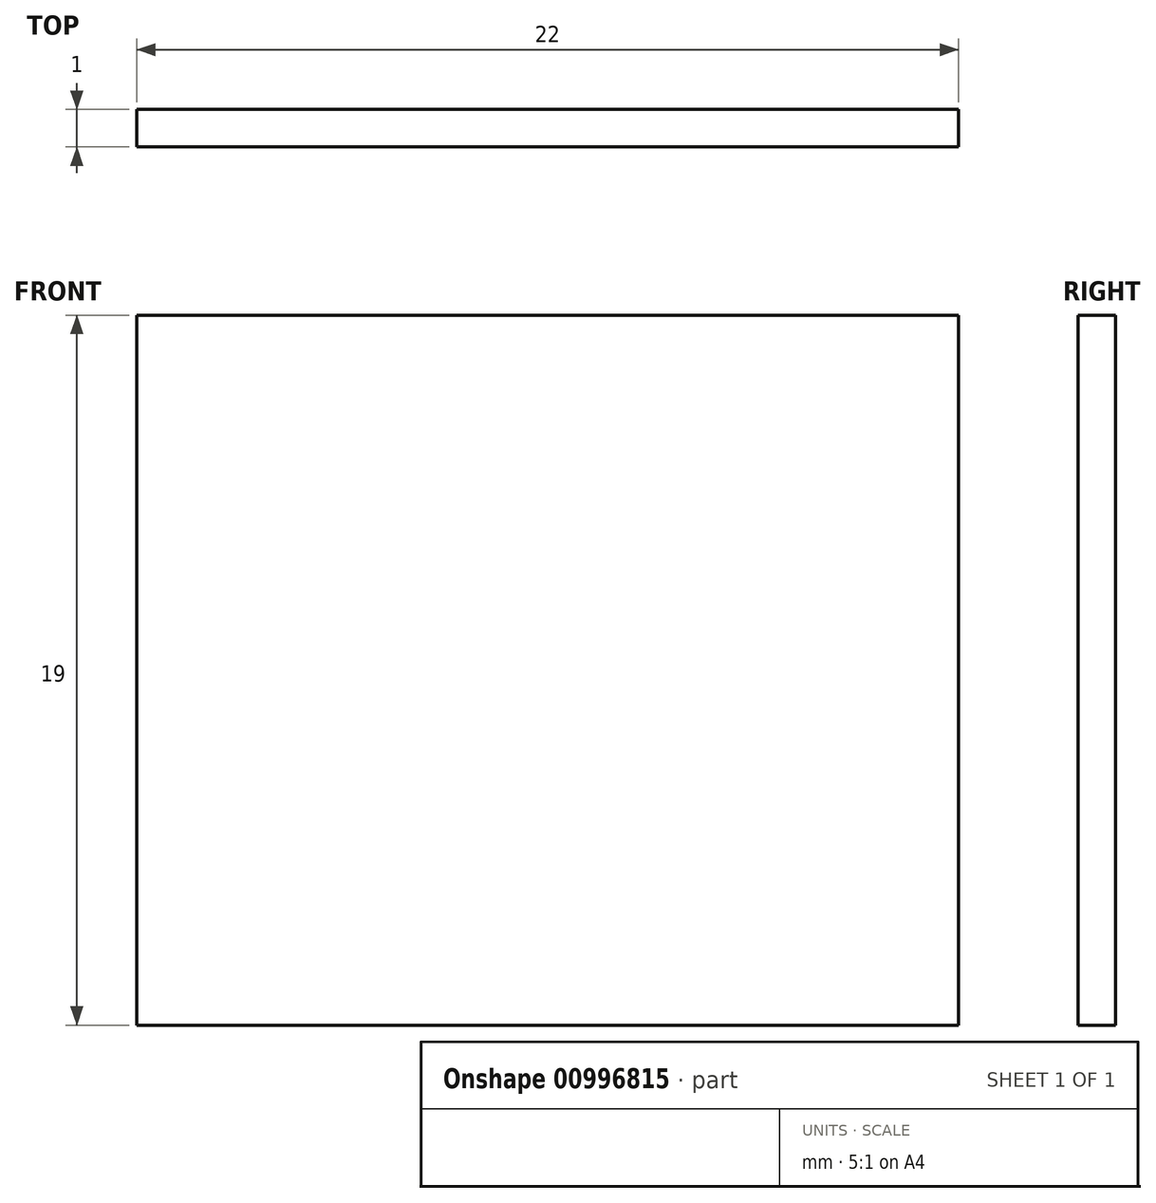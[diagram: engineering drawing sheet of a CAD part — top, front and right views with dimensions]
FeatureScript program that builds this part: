
annotation { "Feature Type Name" : "Feature", "Feature Type Description" : "" }
export const myFeature = defineFeature(function(context is Context, id is Id, definition is map)
    precondition{}
    {
        {
            var Q0;
            Q0=qCreatedBy(makeId("Front.planeOp"),FACE);
            var sketch = newSketch(context, id + "F0", { "sketchPlane" : qUnion([Q0])});
            skLineSegment(sketch, "E0.bottom", {"start": v(11, 9.5) * mm, "end": v(-11, 9.5) * mm});
            skLineSegment(sketch, "E0.top", {"start": v(11, -9.5) * mm, "end": v(-11, -9.5) * mm});
            skLineSegment(sketch, "E0.left", {"start": v(11, 9.5) * mm, "end": v(11, -9.5) * mm});
            skLineSegment(sketch, "E0.right", {"start": v(-11, 9.5) * mm, "end": v(-11, -9.5) * mm});
            skPoint(sketch, "E0.middle", {"position": v(0, 0) * mm});
            skSolve(sketch);
        }
        {
            var Q0;
            Q0=makeQuery(id+"F0.imprint","IMPRINT",FACE,{"disambiguationData":[TD([[makeQuery(id+"F0.imprint","IMPRINT",EDGE,{"derivedFrom":sQuery(id+"F0.wireOp",EDGE,"E0.bottom")}),1.0]])]});
            extrude(context, id + "F1", {"entities" : qUnion([Q0]), "depth" : 1 * mm, "offsetDistance" : 25 * mm});
        }
    });
